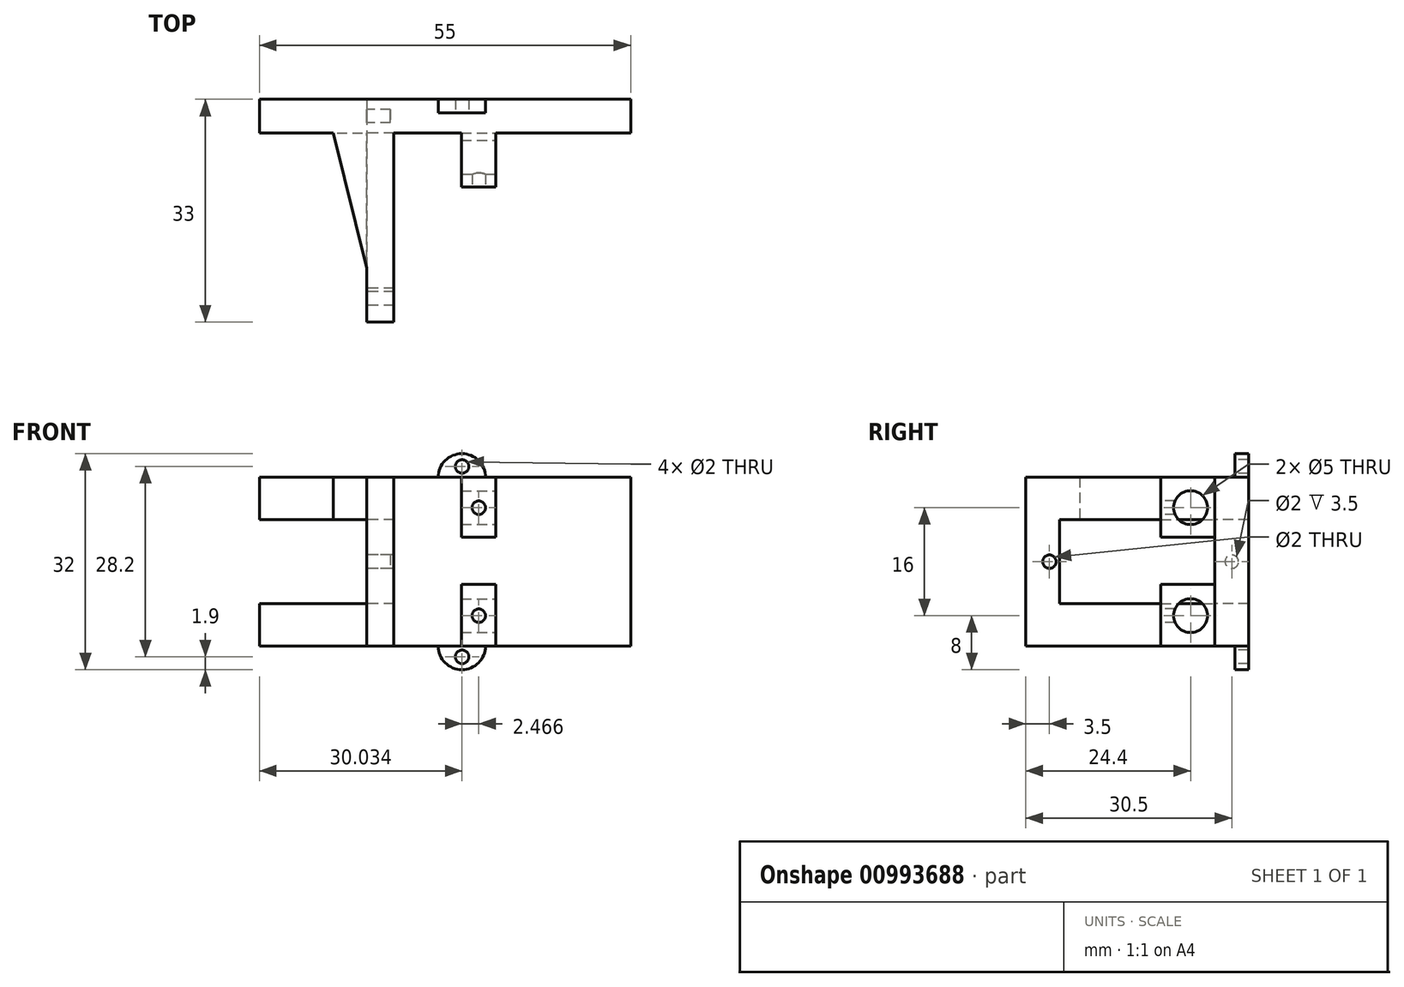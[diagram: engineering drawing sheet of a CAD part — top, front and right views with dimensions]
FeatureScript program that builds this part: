
annotation { "Feature Type Name" : "Feature", "Feature Type Description" : "" }
export const myFeature = defineFeature(function(context is Context, id is Id, definition is map)
    precondition{}
    {
        {
            var Q0;
            Q0=qCreatedBy(makeId("Front.planeOp"),FACE);
            var sketch = newSketch(context, id + "F0", { "sketchPlane" : qUnion([Q0])});
            skLineSegment(sketch, "E0.bottom", {"start": v(-27.5, 12.5) * mm, "end": v(27.5, 12.5) * mm});
            skLineSegment(sketch, "E0.top", {"start": v(-27.5, -12.5) * mm, "end": v(27.5, -12.5) * mm});
            skLineSegment(sketch, "E0.left", {"start": v(-27.5, 12.5) * mm, "end": v(-27.5, -12.5) * mm});
            skLineSegment(sketch, "E0.right", {"start": v(27.5, 12.5) * mm, "end": v(27.5, -12.5) * mm});
            skPoint(sketch, "E0.middle", {"position": v(0, 0) * mm});
            skSolve(sketch);
        }
        {
            var Q0;
            Q0=makeQuery(id+"F0.imprint","IMPRINT",FACE,{"disambiguationData":[TD([[makeQuery(id+"F0.imprint","IMPRINT",EDGE,{"derivedFrom":sQuery(id+"F0.wireOp",EDGE,"E0.bottom")}),-1.0]])]});
            extrude(context, id + "F1", {"entities" : qUnion([Q0]), "depth" : 5 * mm});
        }
        {
            var Q0;
            Q0=makeQuery(id+"F1.opExtrude","CAP_FACE",FACE,{"disambiguationData":[OSD([sQuery(id+"F0.wireOp",EDGE,"E0.bottom"),sQuery(id+"F0.wireOp",EDGE,"E0.top"),sQuery(id+"F0.wireOp",EDGE,"E0.left"),sQuery(id+"F0.wireOp",EDGE,"E0.right")])],"isStart":false});
            var sketch = newSketch(context, id + "F2", { "sketchPlane" : qUnion([Q0])});
            skLineSegment(sketch, "E1", {"start": v(-11.58, 6.25) * mm, "end": v(-11.58, -6.25) * mm});
            skLineSegment(sketch, "E2", {"start": v(-11.58, 6.25) * mm, "end": v(-27.5, 6.25) * mm});
            skLineSegment(sketch, "E3", {"start": v(-11.58, -6.25) * mm, "end": v(-27.5, -6.25) * mm});
            skSolve(sketch);
        }
        {
            var Q0;
            Q0=makeQuery(id+"F2.imprint","IMPRINT",FACE,{"disambiguationData":[TD([[makeQuery(id+"F2.imprint","IMPRINT",EDGE,{"derivedFrom":sQuery(id+"F2.wireOp",EDGE,"E1")}),-1.0]])]});
            extrude(context, id + "F3", {"entities" : qUnion([Q0]), "operationType" : NewBodyOperationType.REMOVE, "endBound" : BoundingType.THROUGH_ALL, "oppositeDirection" : true, "depth" : 25 * mm});
        }
        {
            var Q0;
            Q0=makeQuery(id+"F3.boolean.opBoolean","COPY",FACE,{"derivedFrom":makeQuery(id+"F3.opExtrude","SWEPT_FACE",FACE,{"disambiguationData":[OSD([sQuery(id+"F2.wireOp",EDGE,"E1")])]})});
            var sketch = newSketch(context, id + "F4", { "sketchPlane" : qUnion([Q0])});
            skCircle(sketch, "E4", {"center": v(2.5, 0) * mm, "radius": 1 * mm});
            skSolve(sketch);
        }
        {
            var Q0;
            Q0=makeQuery(id+"F4.imprint","IMPRINT",FACE,{"disambiguationData":[TD([[makeQuery(id+"F4.imprint","IMPRINT",EDGE,{"derivedFrom":sQuery(id+"F4.wireOp",EDGE,"E4")}),1.0]])]});
            extrude(context, id + "F5", {"entities" : qUnion([Q0]), "operationType" : NewBodyOperationType.REMOVE, "oppositeDirection" : true, "depth" : 3.5 * mm});
        }
        {
            var Q0;
            Q0=makeQuery(id+"F1.opExtrude","CAP_FACE",FACE,{"disambiguationData":[OSD([sQuery(id+"F0.wireOp",EDGE,"E0.bottom"),sQuery(id+"F0.wireOp",EDGE,"E0.top"),sQuery(id+"F0.wireOp",EDGE,"E0.left"),sQuery(id+"F0.wireOp",EDGE,"E0.right")])],"isStart":false});
            var sketch = newSketch(context, id + "F6", { "sketchPlane" : qUnion([Q0])});
            skLineSegment(sketch, "E5.bottom", {"start": v(-11.58, 12.5) * mm, "end": v(-7.58, 12.5) * mm});
            skLineSegment(sketch, "E5.top", {"start": v(-11.58, -12.5) * mm, "end": v(-7.58, -12.5) * mm});
            skLineSegment(sketch, "E5.left", {"start": v(-11.58, 12.5) * mm, "end": v(-11.58, -12.5) * mm});
            skLineSegment(sketch, "E5.right", {"start": v(-7.58, 12.5) * mm, "end": v(-7.58, -12.5) * mm});
            skSolve(sketch);
        }
        {
            var Q0;
            {var subQ4=sQuery(id+"F6.wireOp",EDGE,"E5.bottom");Q0=makeQuery(id+"F6.imprint","IMPRINT",FACE,{"disambiguationData":[TD([[makeQuery(id+"F6.imprint","IMPRINT",EDGE,{"derivedFrom":subQ4}),-1.0]])]});}
            extrude(context, id + "F7", {"entities" : qUnion([Q0]), "operationType" : NewBodyOperationType.ADD, "depth" : 28 * mm});
        }
        {
            var Q0;
            Q0=makeQuery(id+"F7.boolean.opBoolean","MERGE",FACE,{"derivedFrom":[makeQuery(id+"F3.boolean.opBoolean","COPY",FACE,{"derivedFrom":makeQuery(id+"F3.opExtrude","SWEPT_FACE",FACE,{"disambiguationData":[OSD([sQuery(id+"F2.wireOp",EDGE,"E1")])]})}),makeQuery(id+"F7.opExtrude","SWEPT_FACE",FACE,{"disambiguationData":[OSD([sQuery(id+"F6.wireOp",EDGE,"E5.left")])]})]});
            var sketch = newSketch(context, id + "F8", { "sketchPlane" : qUnion([Q0])});
            skLineSegment(sketch, "E6.bottom", {"start": v(5, 6.25) * mm, "end": v(28, 6.25) * mm});
            skLineSegment(sketch, "E6.top", {"start": v(5, -6.25) * mm, "end": v(28, -6.25) * mm});
            skLineSegment(sketch, "E6.left", {"start": v(5, 6.25) * mm, "end": v(5, -6.25) * mm});
            skLineSegment(sketch, "E6.right", {"start": v(28, 6.25) * mm, "end": v(28, -6.25) * mm});
            skLineSegment(sketch, "E7.bottom", {"start": v(5, -6.25) * mm, "end": v(5, -6.25) * mm});
            skLineSegment(sketch, "E7.top", {"start": v(5, -6.25) * mm, "end": v(5, -6.25) * mm});
            skLineSegment(sketch, "E7.left", {"start": v(5, -6.25) * mm, "end": v(5, -6.25) * mm});
            skSolve(sketch);
        }
        {
            var Q0;
            Q0=makeQuery(id+"F8.imprint","IMPRINT",FACE,{"disambiguationData":[TD([[makeQuery(id+"F8.imprint","IMPRINT",EDGE,{"derivedFrom":sQuery(id+"F8.wireOp",EDGE,"E6.bottom")}),-1.0]])]});
            extrude(context, id + "F9", {"entities" : qUnion([Q0]), "operationType" : NewBodyOperationType.REMOVE, "endBound" : BoundingType.THROUGH_ALL, "oppositeDirection" : true, "depth" : 25 * mm});
        }
        {
            var Q0;
            {var subQ0=sQuery(id+"F6.wireOp",EDGE,"E5.left");var subQ1=makeQuery(id+"F7.opExtrude","SWEPT_FACE",FACE,{"disambiguationData":[OSD([subQ0])]});var subQ4=sQuery(id+"F0.wireOp",EDGE,"E0.bottom");var subQ6=makeQuery(id+"F3.boolean.opBoolean","COPY",FACE,{"derivedFrom":makeQuery(id+"F3.opExtrude","SWEPT_FACE",FACE,{"disambiguationData":[OSD([sQuery(id+"F2.wireOp",EDGE,"E1")])]})});Q0=makeQuery(id+"F9.boolean.opBoolean","SPLIT",FACE,{"disambiguationData":[TD([makeQuery(id+"F1.opExtrude","SWEPT_FACE",FACE,{"disambiguationData":[OSD([subQ4])]})])],"derivedFrom":makeQuery(id+"F7.boolean.opBoolean","MERGE",FACE,{"derivedFrom":[subQ6,subQ1]})});}
            var sketch = newSketch(context, id + "F10", { "sketchPlane" : qUnion([Q0])});
            skCircle(sketch, "E8", {"center": v(29.5, 0) * mm, "radius": 1 * mm});
            skSolve(sketch);
        }
        {
            var Q0;
            Q0=makeQuery(id+"F10.imprint","IMPRINT",FACE,{"disambiguationData":[TD([[makeQuery(id+"F10.imprint","IMPRINT",EDGE,{"derivedFrom":sQuery(id+"F10.wireOp",EDGE,"E8")}),1.0]])]});
            extrude(context, id + "F11", {"entities" : qUnion([Q0]), "operationType" : NewBodyOperationType.REMOVE, "endBound" : BoundingType.THROUGH_ALL, "oppositeDirection" : true, "depth" : 25 * mm});
        }
        {
            var Q0;
            {var subQ0=sQuery(id+"F0.wireOp",EDGE,"E0.right");var subQ1=sQuery(id+"F0.wireOp",EDGE,"E0.top");var subQ2=sQuery(id+"F0.wireOp",EDGE,"E0.bottom");Q0=makeQuery(id+"F9.boolean.opBoolean","MERGE",FACE,{"derivedFrom":[makeQuery(id+"F7.boolean.opBoolean","SPLIT",FACE,{"disambiguationData":[TD([makeQuery(id+"F1.opExtrude","SWEPT_FACE",FACE,{"disambiguationData":[OSD([subQ0])]})])],"derivedFrom":makeQuery(id+"F1.opExtrude","CAP_FACE",FACE,{"disambiguationData":[OSD([subQ2,subQ1,sQuery(id+"F0.wireOp",EDGE,"E0.left"),subQ0])],"isStart":false})}),makeQuery(id+"F9.opExtrude","SWEPT_FACE",FACE,{"disambiguationData":[OSD([sQuery(id+"F8.wireOp",EDGE,"E6.left")])]})]});}
            var sketch = newSketch(context, id + "F12", { "sketchPlane" : qUnion([Q0])});
            skLineSegment(sketch, "E9.bottom", {"start": v(2.42, -12.5) * mm, "end": v(7.5, -12.5) * mm});
            skLineSegment(sketch, "E9.top", {"start": v(2.42, -3.36) * mm, "end": v(7.5, -3.36) * mm});
            skLineSegment(sketch, "E9.left", {"start": v(2.42, -12.5) * mm, "end": v(2.42, -3.36) * mm});
            skLineSegment(sketch, "E9.right", {"start": v(7.5, -12.5) * mm, "end": v(7.5, -3.36) * mm});
            skLineSegment(sketch, "E10.bottom", {"start": v(2.42, 12.5) * mm, "end": v(7.5, 12.5) * mm});
            skLineSegment(sketch, "E10.top", {"start": v(2.42, 3.64) * mm, "end": v(7.5, 3.64) * mm});
            skLineSegment(sketch, "E10.left", {"start": v(2.42, 12.5) * mm, "end": v(2.42, 3.64) * mm});
            skLineSegment(sketch, "E10.right", {"start": v(7.5, 12.5) * mm, "end": v(7.5, 3.64) * mm});
            skSolve(sketch);
        }
        {
            var Q0;
            Q0=makeQuery(id+"F12.imprint","IMPRINT",FACE,{"disambiguationData":[TD([[makeQuery(id+"F12.imprint","IMPRINT",EDGE,{"derivedFrom":sQuery(id+"F12.wireOp",EDGE,"E10.bottom")}),-1.0]])]});
            var Q1;
            Q1=makeQuery(id+"F12.imprint","IMPRINT",FACE,{"disambiguationData":[TD([[makeQuery(id+"F12.imprint","IMPRINT",EDGE,{"derivedFrom":sQuery(id+"F12.wireOp",EDGE,"E9.bottom")}),1.0]])]});
            extrude(context, id + "F13", {"entities" : qUnion([Q0, Q1]), "operationType" : NewBodyOperationType.ADD, "depth" : 8 * mm});
        }
        {
            var Q0;
            Q0=makeQuery(id+"F13.opExtrude","SWEPT_FACE",FACE,{"disambiguationData":[OSD([sQuery(id+"F12.wireOp",EDGE,"E10.right")])]});
            var sketch = newSketch(context, id + "F14", { "sketchPlane" : qUnion([Q0])});
            skCircle(sketch, "E11", {"center": v(-8.6, 8) * mm, "radius": 2.5 * mm});
            skCircle(sketch, "E12", {"center": v(-8.6, -8) * mm, "radius": 2.5 * mm});
            skSolve(sketch);
        }
        {
            var Q0;
            Q0=makeQuery(id+"F14.imprint","IMPRINT",FACE,{"disambiguationData":[TD([[makeQuery(id+"F14.imprint","IMPRINT",EDGE,{"derivedFrom":sQuery(id+"F14.wireOp",EDGE,"E11")}),1.0]])]});
            var Q1;
            Q1=makeQuery(id+"F14.imprint","IMPRINT",FACE,{"disambiguationData":[TD([[makeQuery(id+"F14.imprint","IMPRINT",EDGE,{"derivedFrom":sQuery(id+"F14.wireOp",EDGE,"E12")}),1.0]])]});
            extrude(context, id + "F15", {"entities" : qUnion([Q0, Q1]), "operationType" : NewBodyOperationType.REMOVE, "oppositeDirection" : true, "depth" : 10 * mm});
        }
        {
            var Q0;
            {var subQ0=sQuery(id+"F0.wireOp",EDGE,"E0.bottom");var subQ1=sQuery(id+"F6.wireOp",EDGE,"E5.left");Q0=makeQuery(id+"F7.boolean.opBoolean","SPLIT",EDGE,{"disambiguationData":[TD([makeQuery(id+"F1.opExtrude","SWEPT_FACE",FACE,{"disambiguationData":[OSD([subQ0])]})])],"derivedFrom":makeQuery(id+"F7.opExtrude","CAP_EDGE",EDGE,{"disambiguationData":[OSD([subQ1])],"isStart":true})});}
            var Q1;
            {var subQ0=sQuery(id+"F0.wireOp",EDGE,"E0.top");var subQ1=sQuery(id+"F6.wireOp",EDGE,"E5.left");Q1=makeQuery(id+"F7.boolean.opBoolean","SPLIT",EDGE,{"disambiguationData":[TD([makeQuery(id+"F1.opExtrude","SWEPT_FACE",FACE,{"disambiguationData":[OSD([subQ0])]})])],"derivedFrom":makeQuery(id+"F7.opExtrude","CAP_EDGE",EDGE,{"disambiguationData":[OSD([subQ1])],"isStart":true})});}
            chamfer(context, id + "F16", {"entities" : qUnion([Q0, Q1]), "chamferType" : ChamferType.TWO_OFFSETS, "width1" : 20 * mm, "oppositeDirection" : false, "width2" : 5 * mm, "tangentPropagation" : true});
        }
        {
            var Q0;
            Q0=makeQuery(id+"F13.opExtrude","CAP_FACE",FACE,{"disambiguationData":[OSD([sQuery(id+"F12.wireOp",EDGE,"E10.bottom"),sQuery(id+"F12.wireOp",EDGE,"E10.top"),sQuery(id+"F12.wireOp",EDGE,"E10.left"),sQuery(id+"F12.wireOp",EDGE,"E10.right")])],"isStart":false});
            var sketch = newSketch(context, id + "F17", { "sketchPlane" : qUnion([Q0])});
            skCircle(sketch, "E13", {"center": v(5, 8) * mm, "radius": 1 * mm});
            skCircle(sketch, "E14", {"center": v(5, -8) * mm, "radius": 1 * mm});
            skSolve(sketch);
        }
        {
            var Q0;
            Q0=makeQuery(id+"F17.imprint","IMPRINT",FACE,{"disambiguationData":[TD([[makeQuery(id+"F17.imprint","IMPRINT",EDGE,{"derivedFrom":sQuery(id+"F17.wireOp",EDGE,"E13")}),1.0]])]});
            var Q1;
            Q1=makeQuery(id+"F17.imprint","IMPRINT",FACE,{"disambiguationData":[TD([[makeQuery(id+"F17.imprint","IMPRINT",EDGE,{"derivedFrom":sQuery(id+"F17.wireOp",EDGE,"E14")}),1.0]])]});
            extrude(context, id + "F18", {"entities" : qUnion([Q0, Q1]), "operationType" : NewBodyOperationType.REMOVE, "oppositeDirection" : true, "depth" : 3 * mm});
        }
        {
            var Q0;
            Q0=makeQuery(id+"F1.opExtrude","CAP_FACE",FACE,{"disambiguationData":[OSD([sQuery(id+"F0.wireOp",EDGE,"E0.bottom"),sQuery(id+"F0.wireOp",EDGE,"E0.top"),sQuery(id+"F0.wireOp",EDGE,"E0.left"),sQuery(id+"F0.wireOp",EDGE,"E0.right")])],"isStart":true});
            var sketch = newSketch(context, id + "F19", { "sketchPlane" : qUnion([Q0])});
            skCircle(sketch, "E15", {"center": v(-2.5, 12.5) * mm, "radius": 3.5 * mm});
            skCircle(sketch, "E16", {"center": v(-2.5, -12.5) * mm, "radius": 3.5 * mm});
            skSolve(sketch);
        }
        {
            var Q0;
            {var subQ0=sQuery(id+"F19.wireOp",EDGE,"E16");var subQ1=makeQuery(id+"F1.opExtrude","CAP_EDGE",EDGE,{"disambiguationData":[OSD([sQuery(id+"F0.wireOp",EDGE,"E0.top")])],"isStart":true});var subQ2=makeQuery(id+"F19.imprint","INTERSECT",VERTEX,{"disambiguationData":[OD(0.0)],"derivedFrom":[subQ1,subQ0]});Q0=makeQuery(id+"F19.imprint","IMPRINT",FACE,{"disambiguationData":[TD([[makeQuery(id+"F19.imprint","IMPRINT",EDGE,{"disambiguationData":[TD([[subQ2,1.0]])],"derivedFrom":subQ0}),1.0]])]});}
            var Q1;
            {var subQ0=sQuery(id+"F19.wireOp",EDGE,"E15");var subQ1=makeQuery(id+"F1.opExtrude","CAP_EDGE",EDGE,{"disambiguationData":[OSD([sQuery(id+"F0.wireOp",EDGE,"E0.bottom")])],"isStart":true});var subQ2=makeQuery(id+"F19.imprint","INTERSECT",VERTEX,{"disambiguationData":[OD(0.0)],"derivedFrom":[subQ1,subQ0]});Q1=makeQuery(id+"F19.imprint","IMPRINT",FACE,{"disambiguationData":[TD([[makeQuery(id+"F19.imprint","IMPRINT",EDGE,{"disambiguationData":[TD([[subQ2,-1.0]])],"derivedFrom":subQ0}),1.0]])]});}
            extrude(context, id + "F20", {"entities" : qUnion([Q0, Q1]), "operationType" : NewBodyOperationType.ADD, "oppositeDirection" : true, "depth" : 2 * mm});
        }
        {
            var Q0;
            Q0=makeQuery(id+"F20.opExtrude","CAP_FACE",FACE,{"disambiguationData":[OSD([sQuery(id+"F0.wireOp",EDGE,"E0.bottom"),sQuery(id+"F19.wireOp",EDGE,"E15")])],"isStart":false});
            var sketch = newSketch(context, id + "F21", { "sketchPlane" : qUnion([Q0])});
            skCircle(sketch, "E17", {"center": v(2.53, 14.1) * mm, "radius": 1 * mm});
            skCircle(sketch, "E18", {"center": v(2.53, -14.1) * mm, "radius": 1 * mm});
            skSolve(sketch);
        }
        {
            var Q0;
            Q0=makeQuery(id+"F21.imprint","IMPRINT",FACE,{"disambiguationData":[TD([[makeQuery(id+"F21.imprint","IMPRINT",EDGE,{"derivedFrom":sQuery(id+"F21.wireOp",EDGE,"E17")}),1.0]])]});
            var Q1;
            Q1=makeQuery(id+"F21.imprint","IMPRINT",FACE,{"disambiguationData":[TD([[makeQuery(id+"F21.imprint","IMPRINT",EDGE,{"derivedFrom":sQuery(id+"F21.wireOp",EDGE,"E18")}),1.0]])]});
            var Q2;
            Q2=sQuery(id+"F21.wireOp",EDGE,"E17");
            var Q3;
            Q3=sQuery(id+"F21.wireOp",EDGE,"E18");
            extrude(context, id + "F22", {"entities" : qUnion([Q0, Q1]), "operationType" : NewBodyOperationType.REMOVE, "surfaceEntities" : qUnion([Q2, Q3]), "endBound" : BoundingType.THROUGH_ALL, "oppositeDirection" : true, "depth" : 25 * mm});
        }
    });
